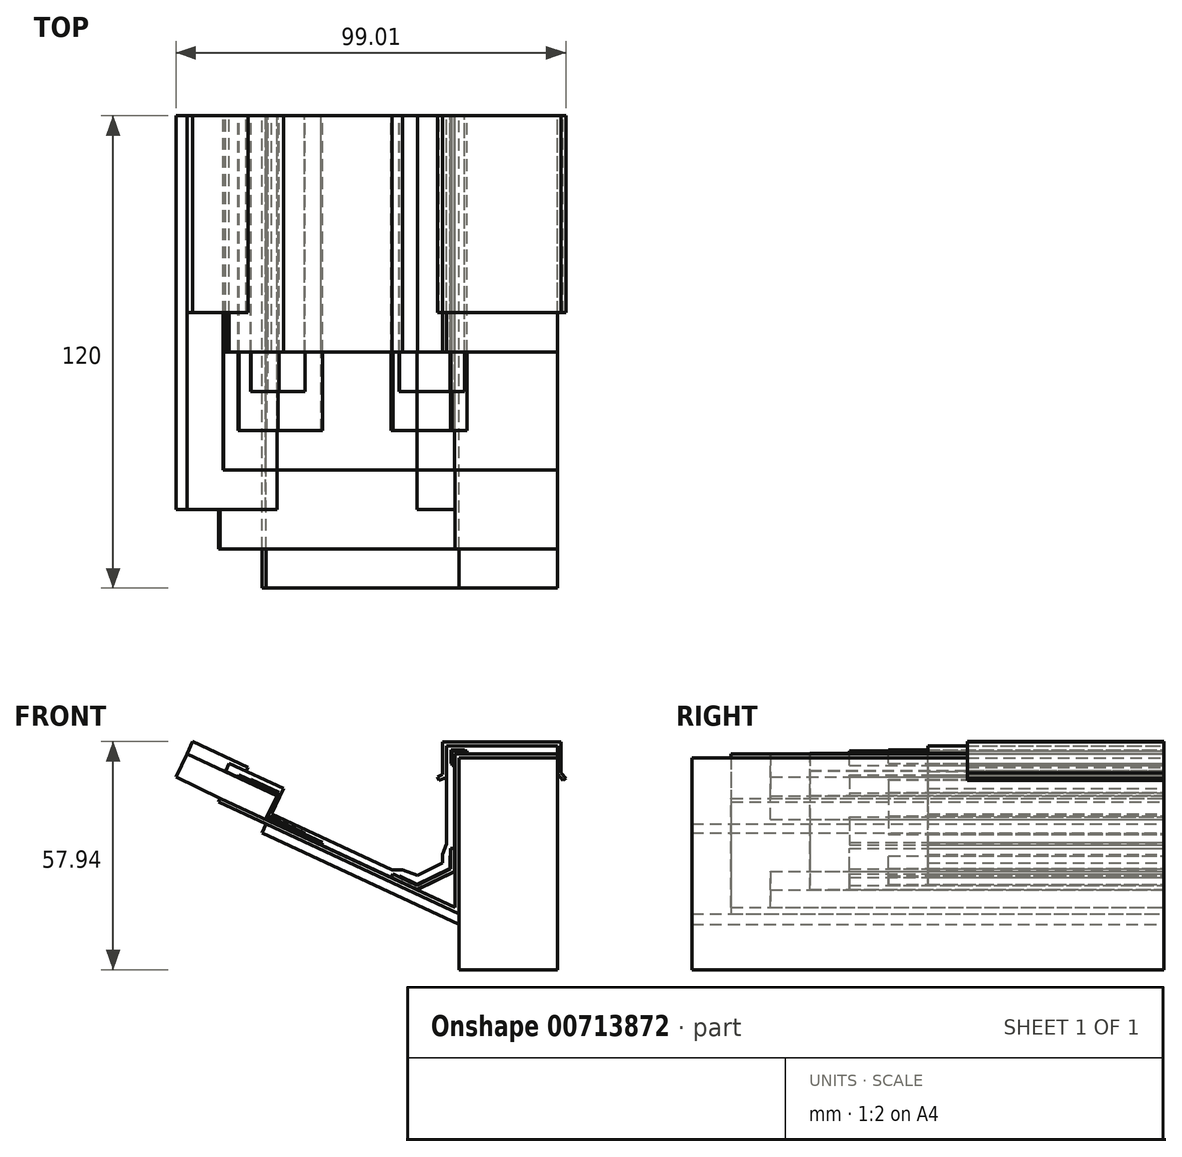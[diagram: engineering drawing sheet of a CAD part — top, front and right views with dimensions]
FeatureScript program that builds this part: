
annotation { "Feature Type Name" : "Feature", "Feature Type Description" : "" }
export const myFeature = defineFeature(function(context is Context, id is Id, definition is map)
    precondition{}
    {
        {
            var Q0;
            Q0=qCreatedBy(makeId("Front.planeOp"),FACE);
            var sketch = newSketch(context, id + "F0", { "sketchPlane" : qUnion([Q0])});
            skLineSegment(sketch, "E0.bottom", {"start": v(37.75, 38.04) * mm, "end": v(62.75, 38.04) * mm});
            skLineSegment(sketch, "E0.top", {"start": v(37.75, -15.78) * mm, "end": v(62.75, -15.78) * mm});
            skLineSegment(sketch, "E0.left", {"start": v(37.75, 38.04) * mm, "end": v(37.75, -15.78) * mm});
            skLineSegment(sketch, "E0.right", {"start": v(62.75, 38.04) * mm, "end": v(62.75, -15.78) * mm});
            skLineSegment(sketch, "E1", {"start": v(62.75, 39.04) * mm, "end": v(36.75, 39.04) * mm});
            skLineSegment(sketch, "E2", {"start": v(36.75, 39.04) * mm, "end": v(36.75, 0) * mm});
            skLineSegment(sketch, "E3", {"start": v(36.75, 0) * mm, "end": v(-22.92, 27.76) * mm});
            skLineSegment(sketch, "E4", {"start": v(-22.92, 27.76) * mm, "end": v(-23.34, 26.86) * mm});
            skLineSegment(sketch, "E5", {"start": v(-23.34, 26.86) * mm, "end": v(37.75, -1.57) * mm});
            skLineSegment(sketch, "E6", {"start": v(37.75, 38.04) * mm, "end": v(37.75, 40.22) * mm, "construction": true});
            skLineSegment(sketch, "E7", {"start": v(-11.3, 22.36) * mm, "end": v(-8.48, 28.43) * mm});
            skLineSegment(sketch, "E8", {"start": v(-8.48, 28.43) * mm, "end": v(-31.34, 39.06) * mm});
            skLineSegment(sketch, "E9", {"start": v(-31.34, 39.06) * mm, "end": v(-34.1, 33.15) * mm});
            skLineSegment(sketch, "E10", {"start": v(-34.1, 33.15) * mm, "end": v(-22.92, 27.76) * mm});
            skLineSegment(sketch, "E11", {"start": v(-11.24, 21.23) * mm, "end": v(-12.29, 18.98) * mm});
            skLineSegment(sketch, "E12", {"start": v(-12.29, 18.98) * mm, "end": v(37.75, -4.3) * mm});
            skLineSegment(sketch, "E13", {"start": v(27.16, 4.46) * mm, "end": v(36.75, 9.19) * mm});
            skLineSegment(sketch, "E14", {"start": v(-22.13, 34.78) * mm, "end": v(-22.09, 34.87) * mm});
            skLineSegment(sketch, "E15", {"start": v(-22.09, 34.87) * mm, "end": v(-8.44, 28.52) * mm});
            skLineSegment(sketch, "E16", {"start": v(-8.44, 28.52) * mm, "end": v(-8.48, 28.43) * mm});
            skLineSegment(sketch, "E17", {"start": v(-11.26, 22.45) * mm, "end": v(27.16, 4.57) * mm});
            skLineSegment(sketch, "E18", {"start": v(27.16, 4.57) * mm, "end": v(36.65, 9.25) * mm});
            skLineSegment(sketch, "E19", {"start": v(36.65, 9.25) * mm, "end": v(36.65, 39.1) * mm});
            skLineSegment(sketch, "E20", {"start": v(36.75, 39.04) * mm, "end": v(36.75, 39.8) * mm, "construction": true});
            skLineSegment(sketch, "E21", {"start": v(27.16, 4.57) * mm, "end": v(27.2, 4.48) * mm, "construction": true});
            skLineSegment(sketch, "E22", {"start": v(-18.36, 33.14) * mm, "end": v(-18.08, 33.74) * mm});
            skLineSegment(sketch, "E23", {"start": v(-18.08, 33.74) * mm, "end": v(-8.15, 29.13) * mm});
            skLineSegment(sketch, "E24", {"start": v(-8.15, 29.13) * mm, "end": v(-8.44, 28.52) * mm});
            skLineSegment(sketch, "E25", {"start": v(-10.98, 23.06) * mm, "end": v(3.07, 16.52) * mm});
            skLineSegment(sketch, "E26", {"start": v(3.07, 16.52) * mm, "end": v(2.79, 15.91) * mm});
            skLineSegment(sketch, "E27", {"start": v(-15.18, 32.4) * mm, "end": v(-15.1, 32.58) * mm});
            skLineSegment(sketch, "E28", {"start": v(-15.1, 32.58) * mm, "end": v(-7.89, 29.22) * mm});
            skLineSegment(sketch, "E29", {"start": v(-7.89, 29.22) * mm, "end": v(-10.67, 23.25) * mm});
            skLineSegment(sketch, "E30", {"start": v(-10.67, 23.25) * mm, "end": v(-1.32, 18.9) * mm});
            skLineSegment(sketch, "E31", {"start": v(-1.32, 18.9) * mm, "end": v(-1.45, 18.62) * mm});
            skLineSegment(sketch, "E32", {"start": v(-8.15, 29.13) * mm, "end": v(-7.97, 29.04) * mm, "construction": true});
            skLineSegment(sketch, "E33", {"start": v(20.57, 7.64) * mm, "end": v(20.99, 8.55) * mm});
            skLineSegment(sketch, "E34", {"start": v(20.99, 8.55) * mm, "end": v(27.15, 5.68) * mm});
            skLineSegment(sketch, "E35", {"start": v(27.15, 5.68) * mm, "end": v(35.65, 9.87) * mm});
            skLineSegment(sketch, "E36", {"start": v(35.65, 9.87) * mm, "end": v(35.65, 15.07) * mm});
            skLineSegment(sketch, "E37", {"start": v(35.65, 15.07) * mm, "end": v(36.65, 15.07) * mm});
            skLineSegment(sketch, "E38", {"start": v(35.65, 9.87) * mm, "end": v(36.1, 8.97) * mm, "construction": true});
            skLineSegment(sketch, "E39", {"start": v(27.15, 5.68) * mm, "end": v(27.6, 4.78) * mm, "construction": true});
            skLineSegment(sketch, "E40", {"start": v(22.39, 7.9) * mm, "end": v(22.54, 7.83) * mm});
            skLineSegment(sketch, "E41", {"start": v(22.54, 7.83) * mm, "end": v(22.62, 8) * mm});
            skLineSegment(sketch, "E42", {"start": v(22.62, 8) * mm, "end": v(27.15, 5.9) * mm});
            skLineSegment(sketch, "E43", {"start": v(27.15, 5.9) * mm, "end": v(35.45, 10) * mm});
            skLineSegment(sketch, "E44", {"start": v(35.45, 10) * mm, "end": v(35.45, 13.11) * mm});
            skLineSegment(sketch, "E45", {"start": v(35.45, 13.11) * mm, "end": v(35.65, 13.11) * mm});
            skLineSegment(sketch, "E46", {"start": v(35.45, 10) * mm, "end": v(35.54, 9.82) * mm, "construction": true});
            skLineSegment(sketch, "E47", {"start": v(27.15, 5.9) * mm, "end": v(27.15, 5.68) * mm, "construction": true});
            skLineSegment(sketch, "E48", {"start": v(35.98, 36.13) * mm, "end": v(35.98, 39.78) * mm});
            skLineSegment(sketch, "E49", {"start": v(35.98, 39.78) * mm, "end": v(39.8, 39.8) * mm});
            skLineSegment(sketch, "E50", {"start": v(35.98, 36.62) * mm, "end": v(35.78, 36.62) * mm});
            skLineSegment(sketch, "E51", {"start": v(35.78, 36.62) * mm, "end": v(35.78, 40) * mm});
            skLineSegment(sketch, "E52", {"start": v(35.78, 40) * mm, "end": v(39.22, 40) * mm});
            skLineSegment(sketch, "E53", {"start": v(39.22, 40) * mm, "end": v(39.22, 39.8) * mm});
            skLineSegment(sketch, "E54", {"start": v(-21.56, 34.62) * mm, "end": v(-20.6, 36.68) * mm});
            skLineSegment(sketch, "E55", {"start": v(-20.6, 36.68) * mm, "end": v(-6.85, 30.28) * mm});
            skLineSegment(sketch, "E56", {"start": v(-6.85, 30.28) * mm, "end": v(-9.89, 23.74) * mm});
            skLineSegment(sketch, "E57", {"start": v(-9.89, 23.74) * mm, "end": v(20.81, 9.62) * mm});
            skLineSegment(sketch, "E58", {"start": v(34.65, 16.2) * mm, "end": v(34.65, 41.1) * mm});
            skLineSegment(sketch, "E59", {"start": v(34.65, 41.1) * mm, "end": v(46.3, 41.1) * mm});
            skLineSegment(sketch, "E60", {"start": v(46.3, 41.1) * mm, "end": v(47.1, 41.1) * mm});
            skLineSegment(sketch, "E61", {"start": v(47.1, 41.1) * mm, "end": v(62.75, 41.1) * mm});
            skLineSegment(sketch, "E62", {"start": v(41.21, 39.1) * mm, "end": v(41.21, 41.1) * mm, "construction": true});
            skLineSegment(sketch, "E63", {"start": v(36.65, 32.37) * mm, "end": v(34.65, 32.37) * mm, "construction": true});
            skLineSegment(sketch, "E64", {"start": v(20.81, 9.62) * mm, "end": v(23.42, 9.62) * mm});
            skLineSegment(sketch, "E65", {"start": v(23.42, 9.62) * mm, "end": v(27.28, 8.2) * mm});
            skLineSegment(sketch, "E66", {"start": v(27.28, 8.2) * mm, "end": v(33.65, 11.34) * mm});
            skLineSegment(sketch, "E67", {"start": v(33.65, 11.34) * mm, "end": v(33.65, 13.5) * mm});
            skLineSegment(sketch, "E68", {"start": v(33.65, 13.5) * mm, "end": v(34.65, 16.2) * mm});
            skLineSegment(sketch, "E69", {"start": v(20.81, 9.62) * mm, "end": v(19.97, 7.8) * mm, "construction": true});
            skLineSegment(sketch, "E70", {"start": v(19.97, 7.8) * mm, "end": v(19.73, 8.1) * mm, "construction": true});
            skLineSegment(sketch, "E71", {"start": v(34.65, 16.2) * mm, "end": v(36.65, 16.2) * mm, "construction": true});
            skLineSegment(sketch, "E72", {"start": v(33.65, 13.5) * mm, "end": v(35.65, 13.5) * mm, "construction": true});
            skLineSegment(sketch, "E73", {"start": v(33.65, 11.34) * mm, "end": v(34.54, 9.54) * mm, "construction": true});
            skLineSegment(sketch, "E74", {"start": v(34.54, 9.54) * mm, "end": v(34.41, 9.65) * mm, "construction": true});
            skLineSegment(sketch, "E75", {"start": v(23.42, 9.62) * mm, "end": v(22.58, 7.8) * mm, "construction": true});
            skLineSegment(sketch, "E76", {"start": v(22.58, 7.8) * mm, "end": v(22.51, 7.96) * mm, "construction": true});
            skLineSegment(sketch, "E77", {"start": v(27.28, 8.2) * mm, "end": v(28.23, 6.44) * mm, "construction": true});
            skLineSegment(sketch, "E78", {"start": v(34.65, 33.12) * mm, "end": v(32.74, 32.27) * mm});
            skLineSegment(sketch, "E79", {"start": v(32.74, 32.27) * mm, "end": v(32.33, 33.18) * mm});
            skLineSegment(sketch, "E80", {"start": v(32.33, 33.18) * mm, "end": v(33.65, 33.77) * mm});
            skLineSegment(sketch, "E81", {"start": v(33.65, 33.77) * mm, "end": v(33.65, 42.1) * mm});
            skLineSegment(sketch, "E82", {"start": v(33.65, 42.1) * mm, "end": v(63.75, 42.1) * mm});
            skLineSegment(sketch, "E83", {"start": v(63.75, 42.1) * mm, "end": v(63.75, 34.16) * mm});
            skLineSegment(sketch, "E84", {"start": v(63.75, 34.16) * mm, "end": v(64.92, 32.86) * mm});
            skLineSegment(sketch, "E85", {"start": v(64.92, 32.86) * mm, "end": v(64.27, 32.27) * mm});
            skLineSegment(sketch, "E86", {"start": v(64.27, 32.27) * mm, "end": v(62.75, 33.95) * mm});
            skLineSegment(sketch, "E87", {"start": v(33.65, 33.77) * mm, "end": v(34.65, 33.77) * mm, "construction": true});
            skLineSegment(sketch, "E88", {"start": v(34.65, 41.1) * mm, "end": v(33.65, 41.1) * mm, "construction": true});
            skLineSegment(sketch, "E89", {"start": v(62.75, 41.1) * mm, "end": v(63.75, 41.1) * mm, "construction": true});
            skLineSegment(sketch, "E90", {"start": v(63.75, 34.16) * mm, "end": v(62.75, 34.16) * mm, "construction": true});
            skLineSegment(sketch, "E91", {"start": v(62.75, 39.04) * mm, "end": v(62.75, 38.04) * mm});
            skLineSegment(sketch, "E92", {"start": v(62.75, 39.14) * mm, "end": v(62.75, 39.04) * mm});
            skLineSegment(sketch, "E93", {"start": v(36.65, 39.1) * mm, "end": v(62.75, 39.14) * mm});
            skLineSegment(sketch, "E94", {"start": v(62.75, 41.1) * mm, "end": v(62.75, 39.14) * mm});
            skLineSegment(sketch, "E95", {"start": v(35.98, 36.13) * mm, "end": v(36.65, 36.13) * mm});
            skLineSegment(sketch, "E96", {"start": v(39.8, 39.8) * mm, "end": v(39.8, 39.1) * mm});
            skLineSegment(sketch, "E97", {"start": v(-16.25, 34.65) * mm, "end": v(-15.8, 35.6) * mm});
            skLineSegment(sketch, "E98", {"start": v(-15.8, 35.6) * mm, "end": v(-29.9, 42.16) * mm});
            skLineSegment(sketch, "E99", {"start": v(-29.9, 42.16) * mm, "end": v(-31.34, 39.06) * mm});
            skSolve(sketch);
        }
        {
            var Q0;
            {var subQ4=sQuery(id+"F0.wireOp",EDGE,"E0.top");Q0=makeQuery(id+"F0.imprint","IMPRINT",FACE,{"disambiguationData":[TD([[makeQuery(id+"F0.imprint","IMPRINT",EDGE,{"derivedFrom":subQ4}),1.0]])]});}
            extrude(context, id + "F1", {"entities" : qUnion([Q0]), "depth" : 120 * mm});
        }
        {
            var Q0;
            {var subQ4=sQuery(id+"F0.wireOp",EDGE,"E11");Q0=makeQuery(id+"F0.imprint","IMPRINT",FACE,{"disambiguationData":[TD([[makeQuery(id+"F0.imprint","IMPRINT",EDGE,{"derivedFrom":subQ4}),1.0]])]});}
            extrude(context, id + "F2", {"entities" : qUnion([Q0]), "depth" : 120 * mm});
        }
        {
            var Q0;
            {var subQ8=sQuery(id+"F0.wireOp",EDGE,"E1");Q0=makeQuery(id+"F0.imprint","IMPRINT",FACE,{"disambiguationData":[TD([[makeQuery(id+"F0.imprint","IMPRINT",EDGE,{"derivedFrom":subQ8}),1.0]])]});}
            extrude(context, id + "F3", {"entities" : qUnion([Q0]), "depth" : 110 * mm});
        }
        {
            var Q0;
            {var subQ9=sQuery(id+"F0.wireOp",EDGE,"E9");Q0=makeQuery(id+"F0.imprint","IMPRINT",FACE,{"disambiguationData":[TD([[makeQuery(id+"F0.imprint","IMPRINT",EDGE,{"derivedFrom":subQ9}),1.0]])]});}
            extrude(context, id + "F4", {"entities" : qUnion([Q0]), "depth" : 100 * mm});
        }
        {
            var Q0;
            {var subQ3=sQuery(id+"F0.wireOp",EDGE,"E13");Q0=makeQuery(id+"F0.imprint","IMPRINT",FACE,{"disambiguationData":[TD([[makeQuery(id+"F0.imprint","IMPRINT",EDGE,{"derivedFrom":subQ3}),-1.0]])]});}
            extrude(context, id + "F5", {"entities" : qUnion([Q0]), "depth" : 100 * mm});
        }
        {
            var Q0;
            {var subQ3=sQuery(id+"F0.wireOp",EDGE,"E14");Q0=makeQuery(id+"F0.imprint","IMPRINT",FACE,{"disambiguationData":[TD([[makeQuery(id+"F0.imprint","IMPRINT",EDGE,{"derivedFrom":subQ3}),-1.0]])]});}
            extrude(context, id + "F6", {"entities" : qUnion([Q0]), "depth" : 90 * mm});
        }
        {
            var Q0;
            {var subQ12=sQuery(id+"F0.wireOp",EDGE,"E1");Q0=makeQuery(id+"F0.imprint","IMPRINT",FACE,{"disambiguationData":[TD([[makeQuery(id+"F0.imprint","IMPRINT",EDGE,{"derivedFrom":subQ12}),-1.0]])]});}
            extrude(context, id + "F7", {"entities" : qUnion([Q0]), "depth" : 90 * mm});
        }
        {
            var Q0;
            {var subQ4=sQuery(id+"F0.wireOp",EDGE,"E22");Q0=makeQuery(id+"F0.imprint","IMPRINT",FACE,{"disambiguationData":[TD([[makeQuery(id+"F0.imprint","IMPRINT",EDGE,{"derivedFrom":subQ4}),-1.0]])]});}
            extrude(context, id + "F8", {"entities" : qUnion([Q0]), "depth" : 80 * mm});
        }
        {
            var Q0;
            {var subQ0=sQuery(id+"F0.wireOp",EDGE,"E26");Q0=makeQuery(id+"F0.imprint","IMPRINT",FACE,{"disambiguationData":[TD([[makeQuery(id+"F0.imprint","IMPRINT",EDGE,{"derivedFrom":subQ0}),-1.0]])]});}
            extrude(context, id + "F9", {"entities" : qUnion([Q0]), "depth" : 80 * mm});
        }
        {
            var Q0;
            {var subQ7=sQuery(id+"F0.wireOp",EDGE,"E18");Q0=makeQuery(id+"F0.imprint","IMPRINT",FACE,{"disambiguationData":[TD([[makeQuery(id+"F0.imprint","IMPRINT",EDGE,{"derivedFrom":subQ7}),1.0]])]});}
            extrude(context, id + "F10", {"entities" : qUnion([Q0]), "depth" : 80 * mm});
        }
        {
            var Q0;
            {var subQ6=sQuery(id+"F0.wireOp",EDGE,"E95");Q0=makeQuery(id+"F0.imprint","IMPRINT",FACE,{"disambiguationData":[TD([[makeQuery(id+"F0.imprint","IMPRINT",EDGE,{"derivedFrom":subQ6}),1.0]])]});}
            extrude(context, id + "F11", {"entities" : qUnion([Q0]), "depth" : 80 * mm});
        }
        {
            var Q0;
            {var subQ1=sQuery(id+"F0.wireOp",EDGE,"E16");Q0=makeQuery(id+"F0.imprint","IMPRINT",FACE,{"disambiguationData":[TD([[makeQuery(id+"F0.imprint","IMPRINT",EDGE,{"derivedFrom":subQ1}),1.0]])]});}
            extrude(context, id + "F12", {"entities" : qUnion([Q0]), "depth" : 70 * mm});
        }
        {
            var Q0;
            {var subQ1=sQuery(id+"F0.wireOp",EDGE,"E35");Q0=makeQuery(id+"F0.imprint","IMPRINT",FACE,{"disambiguationData":[TD([[makeQuery(id+"F0.imprint","IMPRINT",EDGE,{"derivedFrom":subQ1}),1.0]])]});}
            extrude(context, id + "F13", {"entities" : qUnion([Q0]), "depth" : 70 * mm});
        }
        {
            var Q0;
            {var subQ3=sQuery(id+"F0.wireOp",EDGE,"E50");Q0=makeQuery(id+"F0.imprint","IMPRINT",FACE,{"disambiguationData":[TD([[makeQuery(id+"F0.imprint","IMPRINT",EDGE,{"derivedFrom":subQ3}),-1.0]])]});}
            extrude(context, id + "F14", {"entities" : qUnion([Q0]), "depth" : 70 * mm});
        }
        {
            var Q0;
            {var subQ17=sQuery(id+"F0.wireOp",EDGE,"E22");Q0=makeQuery(id+"F0.imprint","IMPRINT",FACE,{"disambiguationData":[TD([[makeQuery(id+"F0.imprint","IMPRINT",EDGE,{"derivedFrom":subQ17}),1.0]])]});}
            extrude(context, id + "F15", {"entities" : qUnion([Q0]), "depth" : 60 * mm});
        }
        {
            var Q0;
            {var subQ3=sQuery(id+"F0.wireOp",EDGE,"E14");Q0=makeQuery(id+"F0.imprint","IMPRINT",FACE,{"disambiguationData":[TD([[makeQuery(id+"F0.imprint","IMPRINT",EDGE,{"derivedFrom":subQ3}),1.0]])]});}
            extrude(context, id + "F16", {"entities" : qUnion([Q0]), "depth" : 50 * mm});
        }
        {
            var Q0;
            {var subQ4=sQuery(id+"F0.wireOp",EDGE,"E59");Q0=makeQuery(id+"F0.imprint","IMPRINT",FACE,{"disambiguationData":[TD([[makeQuery(id+"F0.imprint","IMPRINT",EDGE,{"derivedFrom":subQ4}),1.0]])]});}
            extrude(context, id + "F17", {"entities" : qUnion([Q0]), "depth" : 50 * mm});
        }
    });
